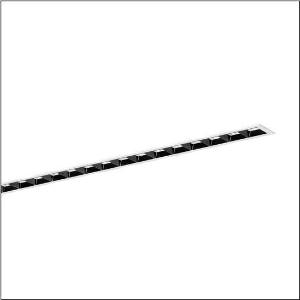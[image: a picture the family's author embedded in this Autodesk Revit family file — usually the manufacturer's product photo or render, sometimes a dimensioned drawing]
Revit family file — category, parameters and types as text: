
# Revit family: silica_r__21_51mx11da44wb_a581
name_source: partatom
category: Lighting Fixtures
units: mm (PartAtom-declared; Revit-internal decimal feet)

## family parameters
Cut with Voids When Loaded = No
Host = Face
Light Source = No
Part Type = Normal
Room Calculation Point = No
Round Connector Dimension = Use Diameter
Shared = No

## types (1)
- --- (1 x LED, 4320 lm, 25.6 W, 4000K)
    Apparent Load = 26 VA
    CIE Flux Codes = 87 99 100 100 100
    Color Rendering = 80
    Color Temperature = 4000K
    Default Elevation = 1800 mm
    Description = Silica® 21, office luminaire, primary light control with darklight reflector, of PMMA, black, CAT 2 (L<= 3000cd/m²), light emission: direct distribution, primary light characteristic: symmetric, installation type: recessed, LED, rated luminous flux: 4.320lm, luminous efficacy: 169lm/W, light colour: 840, colour temperature: 4000K, with terminal, 3+2-pole, max. 2.5mm², mains connection: 220..240V, AC, 50/60Hz, rated input power: 25.6W, luminaire housing, of aluminium, traffic white (RAL 9016), length: 1.228mm, width: 79mm, height: 53mm, protection rating (complete): IP20, insulation class (complete): insulation class I (protective earthing), certification: CE, permissible operating ambient temperature: 0..+35°C, standard: EN 50419, packaging unit: 1 piece
    Height = 0 mm  [stored 0 ft]
    Lamp = 1 x LED
    Lamp Light Flux = 4320 lm
    Lamp Power = 25.6 W
    Lamp count = 1
    Length = 1227 mm
    Luminous efficacy = 169 lm/W
    Manufacturer = Siteco
    ModVariant = No
    Model = 51MX11DA44WB
    Mounting Place = Ceiling
    Mounting Type = Recessed
    Number of Poles = 1
    OnlyDefault = Yes
    Power Factor = 1
    Product Name = Silica® 21
    Product group = office luminaire | ceiling recessed
    ProductGroupID = 401
    Protection Class = Protection class I
    Protection Degree = IP 20
    RLX_Detail_Level = 1
    RLX_Emergency_Light_Flux = 0 lm
    RLX_Emergency_Type = 0
    RLX_Emergency_Type_DB = No
    RlxData = <blob elided: 39177 chars, md5=e0ac2903>
    Socket = socket
    Standby Power = 0 W
    System Light Flux = 4320 lm
    System Power = 26 W
    Type Comments = factory setting: luminous flux: 100 % | dim-lin: 254 | 367 mA
    Type Image = l_1313610.jpg
    URL = http://relux.com
    VarID = @adj_072391
    Voltage = 0 V
    Weight = 0.00 kg
    Width = 79 mm

note: [stored X ft] marks values corroborated as IEEE doubles in the binary element streams (Revit-internal decimal feet)

## geometry (parser evidence)
native form markers: Blend x4, Sweep x12
no freeform markers — native parametric forms only
